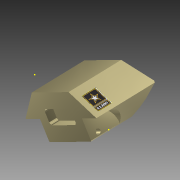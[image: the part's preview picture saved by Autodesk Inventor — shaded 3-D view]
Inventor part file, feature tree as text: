
AUTODESK INVENTOR PART (.ipt)
format: ipt  version: 2015 (Build 190159000, 159)  size: 868,352 bytes
history: native  units: in
note: dims shown in document units (in); Inventor stores cm internally (conversion verified against a paired STEP export)
features: sketch x13, extrude x9, chamfer x4, plane x4, mirror x2, fillet x1, other x1, projected_geometry x1
ambient origin geometry x8: Origin, YZ Plane, XZ Plane, XY Plane, X Axis, Y Axis, Z Axis, Center Point
bodies: Solid1 (feature_tree)
feature tree (35):
  extrude  "Extrusion1"  Depth=4.0in
  chamfer  "Chamfer1"  Distance=6.75in
  chamfer  "Chamfer2"  Distance=1.625in Angle=45.0deg
  chamfer  "Chamfer3"  Distance=1.435in Angle=45.0deg
  chamfer  "Chamfer4"  Distance=1.625in Angle=45.0deg
  plane  "Work Plane1"
  plane  "Work Plane2"
  extrude  "Extrusion2"  [1 undecoded]
  extrude  "Extrusion3"  Depth=0.759in
  mirror  "Mirror1"
  plane  "Work Plane3"
  extrude  "Extrusion4"  Depth=1.38in TaperAngle=0.0deg
  mirror  "Mirror2"
  sketch  "Sketch5"  dims[d23=1.5315in d24=0.25in d25=0.36in]
  extrude  "Extrusion5"  Depth=0.25in
  fillet  "Fillet1"  Radius=0.36in
  plane  "Work Plane4"
  extrude  "Extrusion6"  Depth=2.5in
  extrude  "Extrusion7"  Depth=0.745in
  sketch  "Sketch9"  dims[d50=0.2in d51=0.05in d52=0.0in]
  sketch  "Sketch10"  dims[d53=0.1in d54=0.0in]
  sketch  "Sketch11"  dims[d55=0.1in d56=0.0in]
  extrude  "Extrusion8"  Depth=0.57in TaperAngle=0.0deg
  extrude  "Extrusion9"  Depth=0.05in TaperAngle=0.0deg
  sketch  "Sketch1"  dims[d0=3.06in d1=4.0in d2=6.75in d3=0.0in d4=1.625in d5=0.125in d6=45.0deg d7=1.435in d8=0.125in d9=45.0deg d10=1.625in d11=0.125in d12=45.0deg]
  sketch  "Sketch2"  dims[d13=1.435in d14=0.125in d15=45.0deg d16=-1.38in]
  sketch  "Sketch3"  dims[d17=1.375in d18=0.759in]
  sketch  "Sketch4"  dims[d19=1.38in d20=0.0in d21=1.38in d22=0.0in]
  other  "Image1"
  sketch  "Sketch6"  dims[d26=0.4in d27=0.0in d44=2.5in]
  sketch  "Sketch7"  dims[d45=1.0in d46=0.745in]
  sketch  "Sketch8"  dims[d47=1.03in d48=0.57in d49=0.0in]
  sketch  "Sketch12"  dims[d57=0.05in d58=0.0in]
  projected_geometry  "Projected Loop1"
  sketch  "Sketch13"
note: 1 required parameter value undecoded (feature->parameter linkage not recoverable at this tier; creation-order binding heuristic only, values carry confidence <= 0.55)
